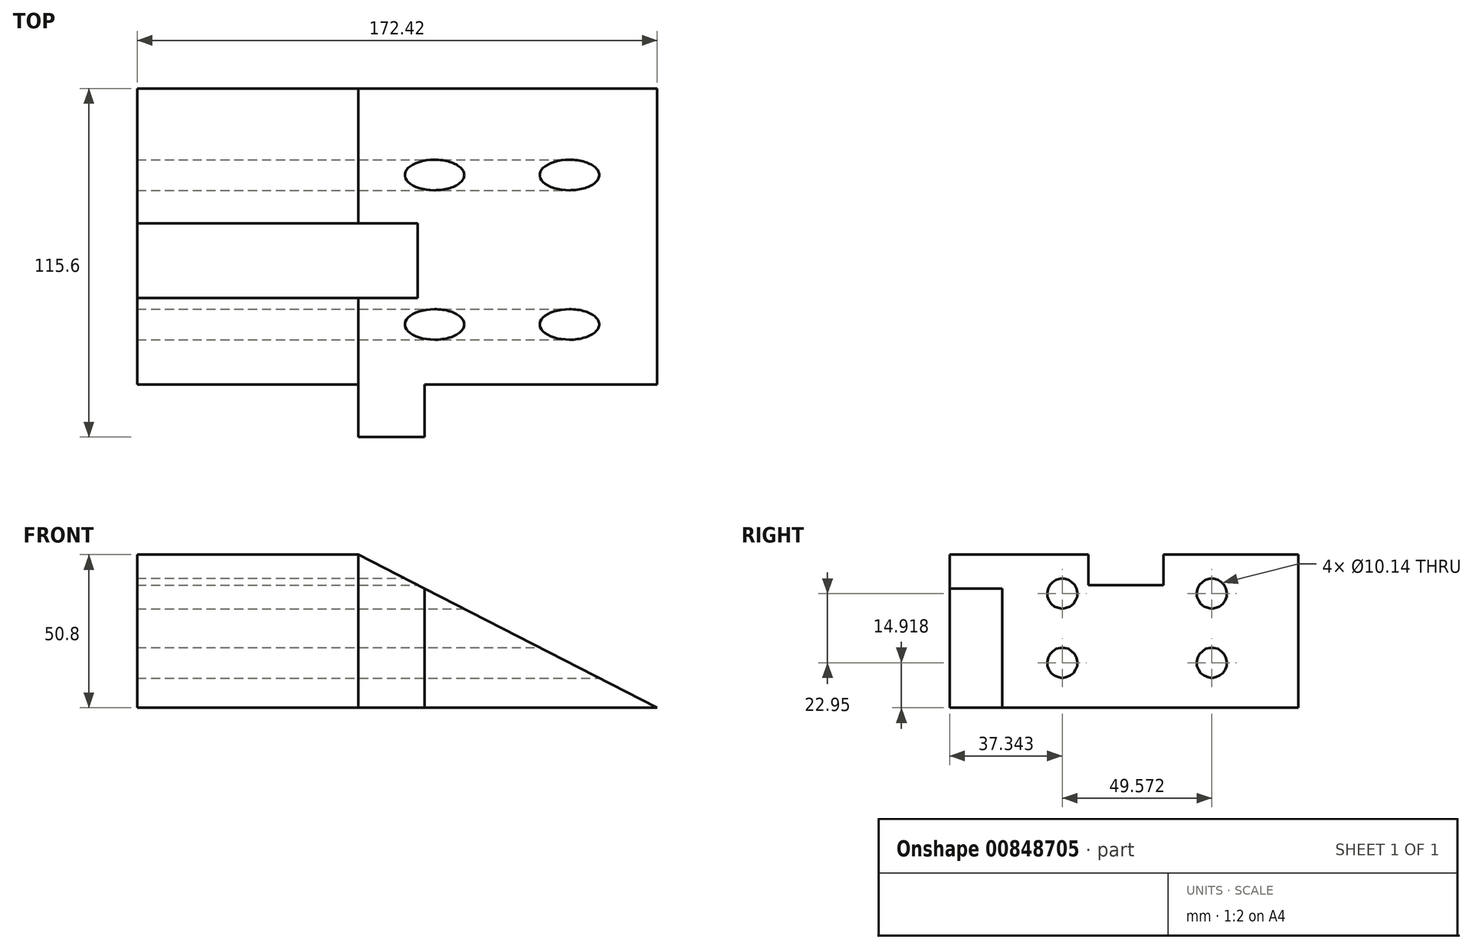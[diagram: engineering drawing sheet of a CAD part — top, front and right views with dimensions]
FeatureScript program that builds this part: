
annotation { "Feature Type Name" : "Feature", "Feature Type Description" : "" }
export const myFeature = defineFeature(function(context is Context, id is Id, definition is map)
    precondition{}
    {
        {
            var Q0;
            Q0=qCreatedBy(makeId("Top.planeOp"),FACE);
            var sketch = newSketch(context, id + "F0", { "sketchPlane" : qUnion([Q0])});
            skLineSegment(sketch, "E0.bottom", {"start": v(-86.2, -49.11) * mm, "end": v(-12.86, -49.11) * mm});
            skLineSegment(sketch, "E0.top", {"start": v(-86.2, 49.11) * mm, "end": v(86.2, 49.11) * mm});
            skLineSegment(sketch, "E0.left", {"start": v(-86.2, -49.11) * mm, "end": v(-86.2, 49.11) * mm});
            skLineSegment(sketch, "E0.right", {"start": v(86.2, -49.11) * mm, "end": v(86.2, 49.11) * mm});
            skPoint(sketch, "E0.middle", {"position": v(0, 0) * mm});
            skLineSegment(sketch, "E1", {"start": v(-12.86, -49.11) * mm, "end": v(-12.86, -66.5) * mm});
            skLineSegment(sketch, "E2", {"start": v(-12.86, -66.5) * mm, "end": v(9.06, -66.5) * mm});
            skLineSegment(sketch, "E3", {"start": v(9.06, -66.5) * mm, "end": v(9.06, -49.11) * mm});
            skLineSegment(sketch, "E4.trimOffspring", {"start": v(9.06, -49.11) * mm, "end": v(86.2, -49.11) * mm});
            skSolve(sketch);
        }
        {
            var Q0;
            Q0=makeQuery(id+"F0.imprint","IMPRINT",FACE,{"disambiguationData":[TD([[makeQuery(id+"F0.imprint","IMPRINT",EDGE,{"derivedFrom":sQuery(id+"F0.wireOp",EDGE,"E0.bottom")}),1.0]])]});
            extrude(context, id + "F1", {"entities" : qUnion([Q0]), "depth" : 50.8 * mm, "offsetDistance" : 25.4 * mm});
        }
        {
            var Q0;
            Q0=qCreatedBy(makeId("Front.planeOp"),FACE);
            var sketch = newSketch(context, id + "F2", { "sketchPlane" : qUnion([Q0])});
            skLineSegment(sketch, "E5.0", {"start": v(-12.86, 50.8) * mm, "end": v(9.06, 50.8) * mm});
            skLineSegment(sketch, "E6.0", {"start": v(9.06, 50.8) * mm, "end": v(86.2, 50.8) * mm});
            skLineSegment(sketch, "E7.0", {"start": v(86.2, 50.8) * mm, "end": v(86.2, 0) * mm});
            skLineSegment(sketch, "E8", {"start": v(86.2, 0) * mm, "end": v(-12.86, 50.8) * mm});
            skSolve(sketch);
        }
        {
            var Q0;
            Q0 = qSketchRegion(id + "F2", true);
            extrude(context, id + "F3", {"entities" : qUnion([Q0]), "operationType" : NewBodyOperationType.REMOVE, "endBound" : BoundingType.THROUGH_ALL, "oppositeDirection" : true, "depth" : 25.4 * mm, "offsetDistance" : 25.4 * mm, "hasSecondDirection" : true, "secondDirectionBound" : SecondDirectionBoundingType.THROUGH_ALL, "secondDirectionOppositeDirection" : false, "secondDirectionDepth" : 25.4 * mm});
        }
        {
            var Q0;
            Q0=qCreatedBy(makeId("Right.planeOp"),FACE);
            var sketch = newSketch(context, id + "F4", { "sketchPlane" : qUnion([Q0])});
            skCircle(sketch, "E9", {"center": v(-29.15, 37.87) * mm, "radius": 5.07 * mm});
            skCircle(sketch, "E10", {"center": v(-29.15, 14.92) * mm, "radius": 5.07 * mm});
            skCircle(sketch, "E11", {"center": v(20.43, 14.92) * mm, "radius": 5.07 * mm});
            skCircle(sketch, "E12", {"center": v(20.43, 37.87) * mm, "radius": 5.07 * mm});
            skLineSegment(sketch, "E13.bottom", {"start": v(-29.15, 37.87) * mm, "end": v(20.43, 37.87) * mm, "construction": true});
            skLineSegment(sketch, "E13.top", {"start": v(-29.15, 14.92) * mm, "end": v(20.43, 14.92) * mm, "construction": true});
            skLineSegment(sketch, "E13.left", {"start": v(-29.15, 37.87) * mm, "end": v(-29.15, 14.92) * mm, "construction": true});
            skLineSegment(sketch, "E13.right", {"start": v(20.43, 37.87) * mm, "end": v(20.43, 14.92) * mm, "construction": true});
            skLineSegment(sketch, "E14.bottom", {"start": v(-20.43, 50.8) * mm, "end": v(4.36, 50.8) * mm});
            skLineSegment(sketch, "E14.top", {"start": v(-20.43, 40.7) * mm, "end": v(4.36, 40.7) * mm});
            skLineSegment(sketch, "E14.left", {"start": v(-20.43, 50.8) * mm, "end": v(-20.43, 40.7) * mm});
            skLineSegment(sketch, "E14.right", {"start": v(4.36, 50.8) * mm, "end": v(4.36, 40.7) * mm});
            skSolve(sketch);
        }
        {
            var Q0;
            Q0 = qSketchRegion(id + "F4", true);
            extrude(context, id + "F5", {"entities" : qUnion([Q0]), "operationType" : NewBodyOperationType.REMOVE, "endBound" : BoundingType.THROUGH_ALL, "oppositeDirection" : true, "depth" : 25.4 * mm, "offsetDistance" : 25.4 * mm, "hasSecondDirection" : true, "secondDirectionBound" : SecondDirectionBoundingType.THROUGH_ALL, "secondDirectionOppositeDirection" : false, "secondDirectionDepth" : 25.4 * mm});
        }
    });
